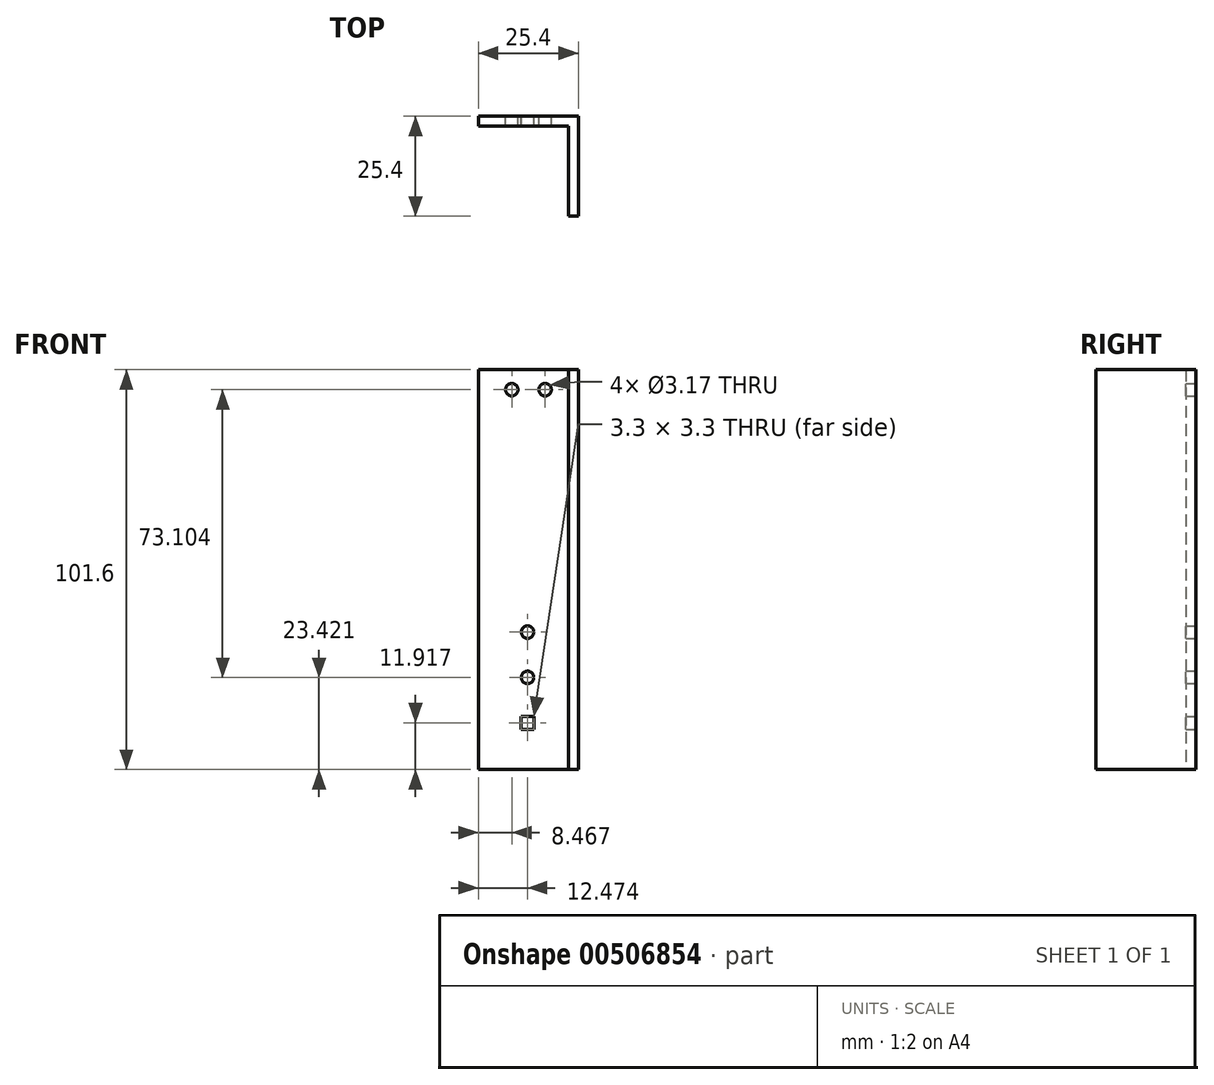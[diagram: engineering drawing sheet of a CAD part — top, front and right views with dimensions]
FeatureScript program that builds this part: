
annotation { "Feature Type Name" : "Feature", "Feature Type Description" : "" }
export const myFeature = defineFeature(function(context is Context, id is Id, definition is map)
    precondition{}
    {
        {
            var Q0;
            Q0=qCreatedBy(makeId("Front.planeOp"),FACE);
            var sketch = newSketch(context, id + "F0", { "sketchPlane" : qUnion([Q0])});
            skLineSegment(sketch, "E0.bottom", {"start": v(-22.25, 44.93) * mm, "end": v(3.15, 44.93) * mm});
            skLineSegment(sketch, "E0.top", {"start": v(-22.25, -56.67) * mm, "end": v(3.15, -56.67) * mm});
            skLineSegment(sketch, "E0.left", {"start": v(-22.25, 44.93) * mm, "end": v(-22.25, -56.67) * mm});
            skLineSegment(sketch, "E0.right", {"start": v(3.15, 44.93) * mm, "end": v(3.15, -56.67) * mm});
            skSolve(sketch);
        }
        {
            var Q0;
            Q0=makeQuery(id+"F0.imprint","IMPRINT",FACE,{"disambiguationData":[TD([[makeQuery(id+"F0.imprint","IMPRINT",EDGE,{"derivedFrom":sQuery(id+"F0.wireOp",EDGE,"E0.bottom")}),-1.0]])]});
            extrude(context, id + "F1", {"entities" : qUnion([Q0]), "depth" : 25.4 * mm, "offsetDistance" : 25.4 * mm});
        }
        {
            var Q0;
            Q0=makeQuery(id+"F1.opExtrude","CAP_FACE",FACE,{"disambiguationData":[OSD([sQuery(id+"F0.wireOp",EDGE,"E0.bottom"),sQuery(id+"F0.wireOp",EDGE,"E0.top"),sQuery(id+"F0.wireOp",EDGE,"E0.left"),sQuery(id+"F0.wireOp",EDGE,"E0.right")])],"isStart":false});
            var Q1;
            Q1=makeQuery(id+"F1.opExtrude","SWEPT_FACE",FACE,{"disambiguationData":[OSD([sQuery(id+"F0.wireOp",EDGE,"E0.bottom")])]});
            var Q2;
            Q2=makeQuery(id+"F1.opExtrude","SWEPT_FACE",FACE,{"disambiguationData":[OSD([sQuery(id+"F0.wireOp",EDGE,"E0.left")])]});
            var Q3;
            Q3=makeQuery(id+"F1.opExtrude","SWEPT_FACE",FACE,{"disambiguationData":[OSD([sQuery(id+"F0.wireOp",EDGE,"E0.top")])]});
            shell(context, id + "F2", {"entities" : qUnion([Q0, Q1, Q2, Q3]), "thickness" : 2.54 * mm});
        }
        {
            var Q0;
            Q0=makeQuery(id+"F1.opExtrude","CAP_FACE",FACE,{"disambiguationData":[OSD([sQuery(id+"F0.wireOp",EDGE,"E0.bottom"),sQuery(id+"F0.wireOp",EDGE,"E0.top"),sQuery(id+"F0.wireOp",EDGE,"E0.left"),sQuery(id+"F0.wireOp",EDGE,"E0.right")])],"isStart":true});
            var sketch = newSketch(context, id + "F3", { "sketchPlane" : qUnion([Q0])});
            skPoint(sketch, "E1", {"position": v(9.78, -44.75) * mm});
            skPoint(sketch, "E2", {"position": v(9.78, -33.25) * mm});
            skPoint(sketch, "E3", {"position": v(9.78, -21.75) * mm});
            skPoint(sketch, "E4", {"position": v(5.32, 39.85) * mm});
            skPoint(sketch, "E5", {"position": v(13.78, 39.85) * mm});
            skLineSegment(sketch, "E6.bottom", {"start": v(11.43, -43.1) * mm, "end": v(8.12, -43.1) * mm});
            skLineSegment(sketch, "E6.top", {"start": v(11.43, -46.4) * mm, "end": v(8.12, -46.4) * mm});
            skLineSegment(sketch, "E6.left", {"start": v(11.43, -43.1) * mm, "end": v(11.43, -46.4) * mm});
            skLineSegment(sketch, "E6.right", {"start": v(8.12, -43.1) * mm, "end": v(8.12, -46.4) * mm});
            skSolve(sketch);
        }
        {
            var Q0;
            Q0=sQuery(id+"F3.wireOp",VERTEX,"E3");
            var Q1;
            Q1=sQuery(id+"F3.wireOp",VERTEX,"E2");
            var Q2;
            Q2=makeQuery(id+"F1.opExtrude","SWEPT_BODY",BODY,{"disambiguationData":[OSD([sQuery(id+"F0.wireOp",EDGE,"E0.bottom"),sQuery(id+"F0.wireOp",EDGE,"E0.top"),sQuery(id+"F0.wireOp",EDGE,"E0.left"),sQuery(id+"F0.wireOp",EDGE,"E0.right")])]});
            hole(context, id + "F4", {"style" : HoleStyle.SIMPLE, "endStyle" : HoleEndStyle.THROUGH, "holeDiameter" : 3.17 * mm, "majorDiameter" : 6.35 * mm, "isTappedThrough" : true, "tappedDepth" : 12.7 * mm, "tapClearance" : 3, "locations" : qUnion([Q0, Q1]), "scope" : qUnion([Q2])});
        }
        {
            var Q0;
            Q0=sQuery(id+"F3.wireOp",VERTEX,"E4");
            var Q1;
            Q1=sQuery(id+"F3.wireOp",VERTEX,"E5");
            var Q2;
            Q2=makeQuery(id+"F1.opExtrude","SWEPT_BODY",BODY,{"disambiguationData":[OSD([sQuery(id+"F0.wireOp",EDGE,"E0.bottom"),sQuery(id+"F0.wireOp",EDGE,"E0.top"),sQuery(id+"F0.wireOp",EDGE,"E0.left"),sQuery(id+"F0.wireOp",EDGE,"E0.right")])]});
            hole(context, id + "F5", {"style" : HoleStyle.SIMPLE, "endStyle" : HoleEndStyle.THROUGH, "holeDiameter" : 3.17 * mm, "majorDiameter" : 6.35 * mm, "isTappedThrough" : true, "tappedDepth" : 12.7 * mm, "tapClearance" : 3, "locations" : qUnion([Q0, Q1]), "scope" : qUnion([Q2])});
        }
        {
            var Q0;
            Q0=makeQuery(id+"F3.imprint","IMPRINT",FACE,{"disambiguationData":[TD([[makeQuery(id+"F3.imprint","IMPRINT",EDGE,{"derivedFrom":sQuery(id+"F3.wireOp",EDGE,"E6.bottom")}),1.0]])]});
            extrude(context, id + "F6", {"entities" : qUnion([Q0]), "operationType" : NewBodyOperationType.REMOVE, "oppositeDirection" : true, "depth" : 10.16 * mm, "offsetDistance" : 25.4 * mm});
        }
    });
